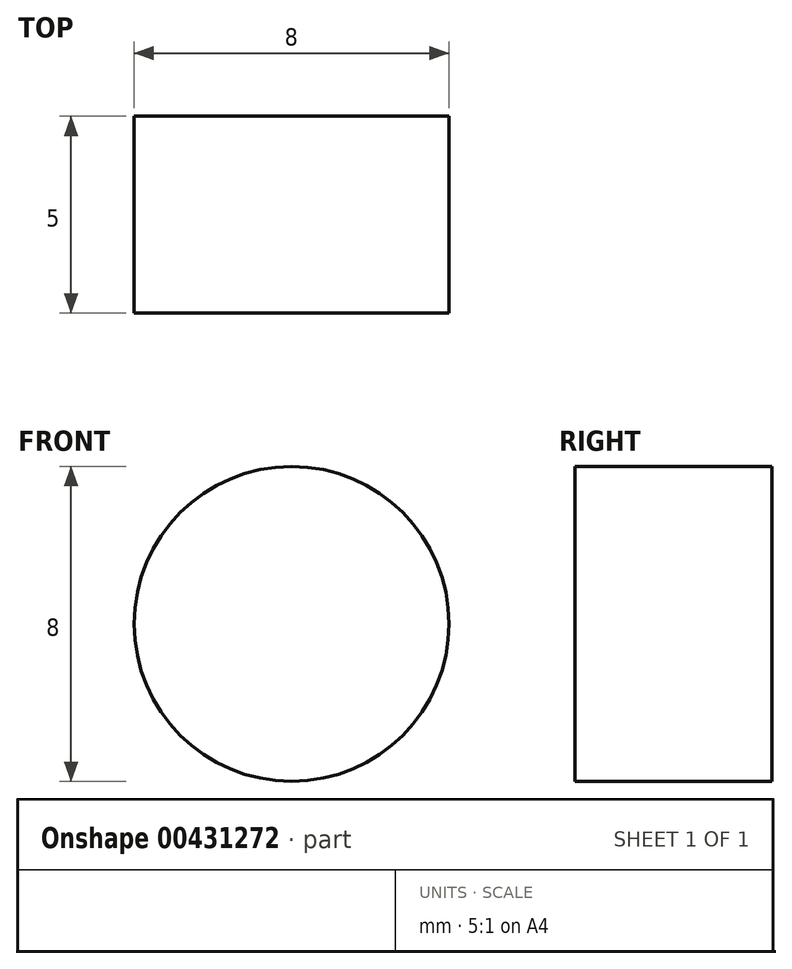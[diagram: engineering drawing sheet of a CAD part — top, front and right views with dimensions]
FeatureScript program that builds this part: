
annotation { "Feature Type Name" : "Feature", "Feature Type Description" : "" }
export const myFeature = defineFeature(function(context is Context, id is Id, definition is map)
    precondition{}
    {
        {
            var Q0;
            Q0=qCreatedBy(makeId("Front.planeOp"),FACE);
            var sketch = newSketch(context, id + "F0", { "sketchPlane" : qUnion([Q0])});
            skCircle(sketch, "E0", {"center": v(0, 0) * mm, "radius": 4 * mm});
            skSolve(sketch);
        }
        {
            var Q0;
            Q0 = qSketchRegion(id + "F0", true);
            extrude(context, id + "F1", {"entities" : qUnion([Q0]), "depth" : 5 * mm});
        }
    });
